# Revit family: Basin-Wall_Hung-DXV-Equility-D2017700X
name_source: partatom
category: Plumbing Fixtures
units: mm (PartAtom-declared; Revit-internal decimal feet)

## family parameters
Cut with Voids When Loaded = No
Host = Face
OmniClass Number = 23.45.05.14.14
OmniClass Title = Sinks/Lavatories
Part Type = Normal
Room Calculation Point = No
Round Connector Dimension = Use Radius
Shared = Yes

## types (2) — shared parameters
ADA Compliant = Yes
ASME A112.18.1/CSA B125.1 = Yes
Assembly Code = D2010310
Basin Shape = Rectangular
CW Connection = Yes
CWFU = 1.5
Cold Water Connection Height = 19 3/4"
Cold Water Connection Width = 4"
Cold Water Diameter = 1/2"
Cold Water Radius = 1/4"
Default Elevation = 34"
Description = Equility 47" Two-Hole, Wall-Mount Trough Lavatory
Finish = Fine Fire Clay-DXV-415-Canvas White
HW Connection = Yes
HWFU = 1.5
Height = 7 1/16"
Hot Water Connection Height = 19 3/4"
Hot Water Connection Width = 4"
Hot Water Diameter = 1/2"
Hot Water Radius = 1/4"
Installation Type = Wall Hung
Length = 17 7/16"
Manufacturer = DXV
Material = Fine Fire Clay-DXV-415-Canvas White
Product Documentation Link = https://dxv01.blob.core.windows.net
Product Page URL = https://www.dxv.com
Revised Date = 11/05/2021
Type Comments = Former LYNDON
URL = https://www.dxv.com
Vent Connection = No
WFU = 2
Warranty Documentation Link = https://www.dxv.com
Waste Connection = Yes
Waste Connection Diameter = 1 1/4"
Waste Connection Height = 18 1/8"
Waste Connection Radius = 5/8"
Width = 46 3/4"

## per-type parameters (varying)
| type | 2 Hole Distance | Single Hole | Single Hole Distance | Two Single Holes |
| D20177002.415 | -6 5/8" | No | -2 1/2" | Yes |
| D20177001.415 | 0" | Yes | 4 1/8" | No |

note: column(s) folded — value = type name in every type: Model

## geometry (parser evidence)
native form markers: Sweep x3
no freeform markers — native parametric forms only
